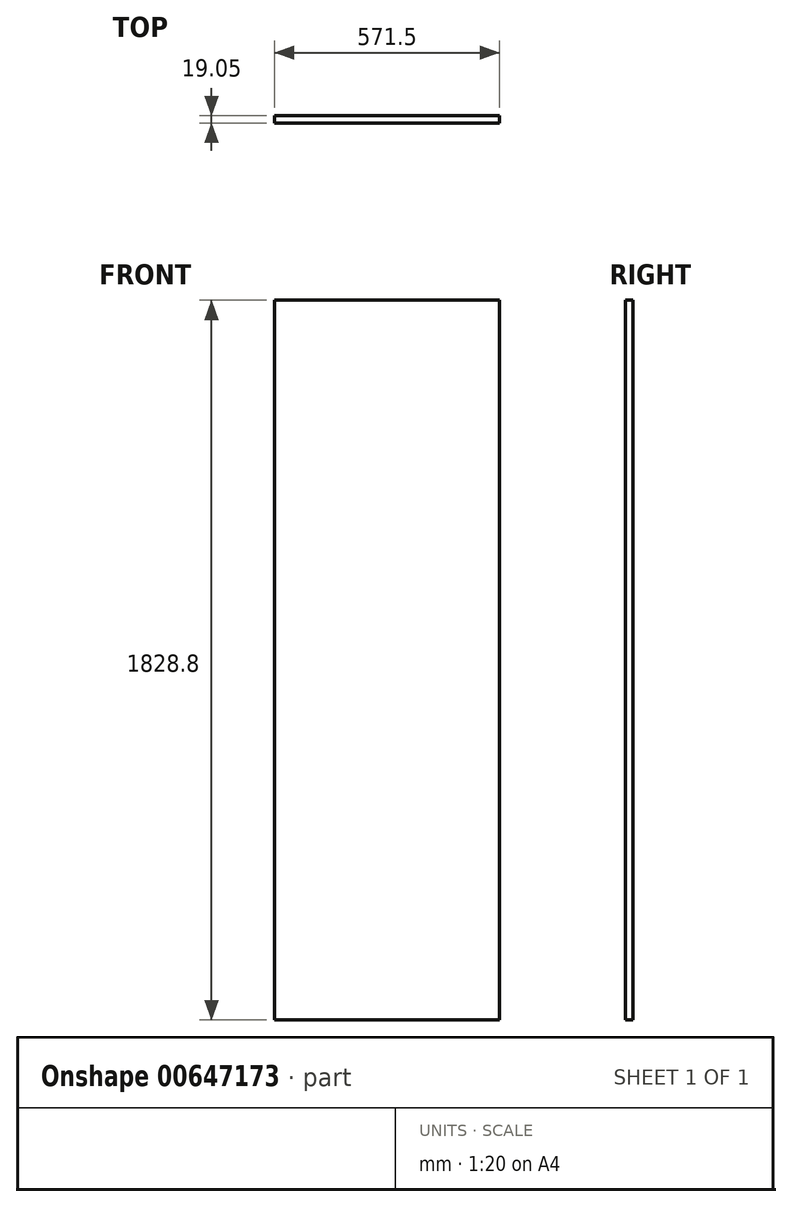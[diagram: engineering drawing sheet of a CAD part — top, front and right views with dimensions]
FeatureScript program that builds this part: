
annotation { "Feature Type Name" : "Feature", "Feature Type Description" : "" }
export const myFeature = defineFeature(function(context is Context, id is Id, definition is map)
    precondition{}
    {
        {
            var Q0;
            Q0=qCreatedBy(makeId("Front.planeOp"),FACE);
            var sketch = newSketch(context, id + "F0", { "sketchPlane" : qUnion([Q0])});
            skLineSegment(sketch, "E0.bottom", {"start": v(285.75, 914.4) * mm, "end": v(-285.75, 914.4) * mm});
            skLineSegment(sketch, "E0.top", {"start": v(285.75, -914.4) * mm, "end": v(-285.75, -914.4) * mm});
            skLineSegment(sketch, "E0.left", {"start": v(285.75, 914.4) * mm, "end": v(285.75, -914.4) * mm});
            skLineSegment(sketch, "E0.right", {"start": v(-285.75, 914.4) * mm, "end": v(-285.75, -914.4) * mm});
            skPoint(sketch, "E0.middle", {"position": v(0, 0) * mm});
            skSolve(sketch);
        }
        {
            var Q0;
            Q0=makeQuery(id+"F0.imprint","IMPRINT",FACE,{"disambiguationData":[TD([[makeQuery(id+"F0.imprint","IMPRINT",EDGE,{"derivedFrom":sQuery(id+"F0.wireOp",EDGE,"E0.bottom")}),1.0]])]});
            extrude(context, id + "F1", {"entities" : qUnion([Q0]), "depth" : 19.05 * mm, "offsetDistance" : 25.4 * mm});
        }
    });
